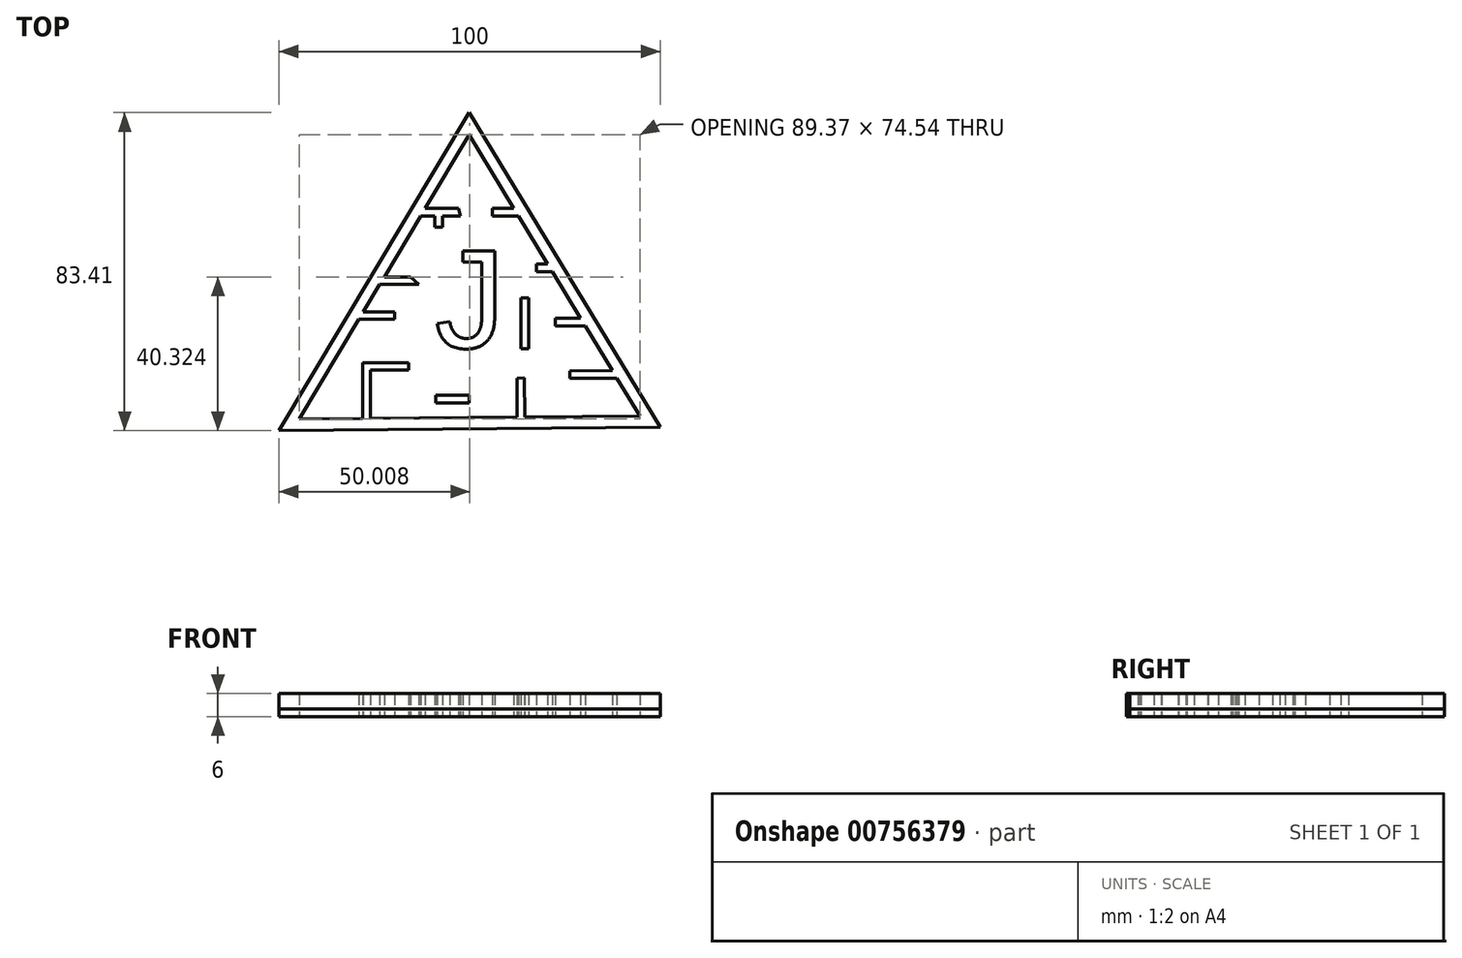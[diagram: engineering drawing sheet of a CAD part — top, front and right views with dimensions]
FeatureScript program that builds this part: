
annotation { "Feature Type Name" : "Feature", "Feature Type Description" : "" }
export const myFeature = defineFeature(function(context is Context, id is Id, definition is map)
    precondition{}
    {
        {
            var Q0;
            Q0=qCreatedBy(makeId("Top.planeOp"),FACE);
            var sketch = newSketch(context, id + "F0", { "sketchPlane" : qUnion([Q0])});
            skLineSegment(sketch, "E0.0", {"start": v(50.1, -33.95) * mm, "end": v(-49.89, -34.84) * mm});
            skLineSegment(sketch, "E0.1", {"start": v(-49.89, -34.84) * mm, "end": v(0, 48.57) * mm});
            skLineSegment(sketch, "E0.2", {"start": v(0, 48.57) * mm, "end": v(50.1, -33.95) * mm});
            skPoint(sketch, "E0.0.midPoint", {"position": v(0.11, -34.4) * mm});
            skText(sketch, "E1", { "text": "J", "fontName": "Arimo-Regular.ttf"});
            skLineSegment(sketch, "E2", {"start": v(6.14, 23.46) * mm, "end": v(11.22, 23.46) * mm});
            skLineSegment(sketch, "E3", {"start": v(-6.97, 21.46) * mm, "end": v(-6.97, 18.51) * mm});
            skLineSegment(sketch, "E4", {"start": v(-25.9, -19) * mm, "end": v(-25.9, -31.62) * mm});
            skLineSegment(sketch, "E5", {"start": v(-25.9, -19) * mm, "end": v(-15.83, -19) * mm});
            skLineSegment(sketch, "E6", {"start": v(-8.82, -25.62) * mm, "end": v(0, -25.55) * mm});
            skLineSegment(sketch, "E7", {"start": v(12.63, -31.28) * mm, "end": v(12.54, -21.07) * mm});
            skLineSegment(sketch, "E8", {"start": v(38.78, -21.07) * mm, "end": v(26.42, -21.18) * mm});
            skLineSegment(sketch, "E9", {"start": v(-15.33, 5.48) * mm, "end": v(-22.27, 5.48) * mm});
            skPoint(sketch, "E9.startSnap0", {"position": v(-22.27, 5.48) * mm});
            skLineSegment(sketch, "E10", {"start": v(15.62, 0) * mm, "end": v(15.62, -13.31) * mm});
            skLineSegment(sketch, "E11", {"start": v(17.7, 8.85) * mm, "end": v(20.6, 8.85) * mm});
            skLineSegment(sketch, "E12", {"start": v(22.63, -5.36) * mm, "end": v(29.23, -5.36) * mm});
            skLineSegment(sketch, "E13.0", {"start": v(6.14, 21.46) * mm, "end": v(12.96, 21.46) * mm});
            skLineSegment(sketch, "E14.0", {"start": v(17.7, 6.85) * mm, "end": v(20.94, 6.85) * mm});
            skLineSegment(sketch, "E15.0", {"start": v(22.63, -7.36) * mm, "end": v(29.56, -7.36) * mm});
            skLineSegment(sketch, "E16.0", {"start": v(13.62, 0) * mm, "end": v(13.62, -13.31) * mm});
            skLineSegment(sketch, "E17.0", {"start": v(37.57, -19.08) * mm, "end": v(26.4, -19.18) * mm});
            skLineSegment(sketch, "E18.0", {"start": v(14.63, -31.3) * mm, "end": v(14.54, -21.05) * mm});
            skLineSegment(sketch, "E19.0", {"start": v(-8.8, -27.62) * mm, "end": v(0.02, -27.55) * mm});
            skLineSegment(sketch, "E20.0", {"start": v(-27.9, -19) * mm, "end": v(-27.9, -31.64) * mm});
            skLineSegment(sketch, "E21.0", {"start": v(-25.5, -17) * mm, "end": v(-15.83, -17) * mm});
            skLineSegment(sketch, "E22", {"start": v(6.14, 23.46) * mm, "end": v(6.14, 21.46) * mm});
            skLineSegment(sketch, "E23.0", {"start": v(-13.24, 3.48) * mm, "end": v(-22.27, 3.48) * mm});
            skLineSegment(sketch, "E24", {"start": v(-6.97, 18.51) * mm, "end": v(-8.97, 18.51) * mm});
            skLineSegment(sketch, "E25", {"start": v(-2.3, 21.46) * mm, "end": v(-2.74, 23.46) * mm});
            skLineSegment(sketch, "E26", {"start": v(17.7, 6.85) * mm, "end": v(17.7, 8.85) * mm});
            skLineSegment(sketch, "E27", {"start": v(22.63, -5.36) * mm, "end": v(22.63, -7.36) * mm});
            skLineSegment(sketch, "E28", {"start": v(13.62, -13.31) * mm, "end": v(15.62, -13.31) * mm});
            skLineSegment(sketch, "E29", {"start": v(13.62, 0) * mm, "end": v(15.62, 0) * mm});
            skLineSegment(sketch, "E30", {"start": v(26.4, -19.18) * mm, "end": v(26.42, -21.18) * mm});
            skLineSegment(sketch, "E31", {"start": v(0, -25.55) * mm, "end": v(0.02, -27.55) * mm});
            skLineSegment(sketch, "E32", {"start": v(-8.82, -25.62) * mm, "end": v(-8.8, -27.62) * mm});
            skLineSegment(sketch, "E33", {"start": v(-27.9, -19) * mm, "end": v(-27.91, -17) * mm});
            skLineSegment(sketch, "E34", {"start": v(-27.91, -17) * mm, "end": v(-25.5, -17) * mm});
            skLineSegment(sketch, "E35", {"start": v(-15.83, -17) * mm, "end": v(-15.83, -19) * mm});
            skLineSegment(sketch, "E36", {"start": v(12.54, -21.07) * mm, "end": v(14.54, -21.05) * mm});
            skLineSegment(sketch, "E37", {"start": v(-13.24, 3.48) * mm, "end": v(-15.33, 5.48) * mm});
            skLineSegment(sketch, "E38", {"start": v(15.62, 0) * mm, "end": v(13.62, 0) * mm});
            skLineSegment(sketch, "E39", {"start": v(-27.76, -3.69) * mm, "end": v(-19.52, -3.69) * mm});
            skLineSegment(sketch, "E40.0", {"start": v(-28.13, -5.69) * mm, "end": v(-19.52, -5.69) * mm});
            skLineSegment(sketch, "E41", {"start": v(-19.52, -5.69) * mm, "end": v(-19.52, -3.69) * mm});
            skLineSegment(sketch, "E42.0", {"start": v(-44.57, -31.79) * mm, "end": v(-28.96, -5.69) * mm});
            skLineSegment(sketch, "E42.1", {"start": v(44.8, -31) * mm, "end": v(14.63, -31.26) * mm});
            skLineSegment(sketch, "E42.2", {"start": v(0.02, 42.76) * mm, "end": v(11.73, 23.46) * mm});
            skLineSegment(sketch, "E43.trimOffspring", {"start": v(-6.97, 21.46) * mm, "end": v(-2.3, 21.46) * mm});
            skLineSegment(sketch, "E44.trimOffspring", {"start": v(-8.97, 21.46) * mm, "end": v(-8.97, 18.51) * mm});
            skPoint(sketch, "E45.orphan", {"position": v(-6.97, 23.46) * mm});
            skLineSegment(sketch, "E46.trimOffspring", {"start": v(-11.52, 23.46) * mm, "end": v(0.02, 42.76) * mm});
            skPoint(sketch, "E47.orphan", {"position": v(-11.2, 23.46) * mm});
            skLineSegment(sketch, "E48", {"start": v(-2.74, 23.46) * mm, "end": v(-11.52, 23.46) * mm});
            skLineSegment(sketch, "E49", {"start": v(-8.97, 21.46) * mm, "end": v(-12.72, 21.46) * mm});
            skLineSegment(sketch, "E50", {"start": v(11.22, 23.46) * mm, "end": v(11.73, 23.46) * mm});
            skLineSegment(sketch, "E51", {"start": v(-22.27, 3.48) * mm, "end": v(-23.47, 3.48) * mm});
            skLineSegment(sketch, "E52", {"start": v(20.94, 6.85) * mm, "end": v(21.82, 6.85) * mm});
            skLineSegment(sketch, "E53.trimOffspring", {"start": v(21.82, 6.85) * mm, "end": v(29.23, -5.36) * mm});
            skLineSegment(sketch, "E54.trimOffspring", {"start": v(-22.27, 5.48) * mm, "end": v(-12.72, 21.46) * mm});
            skLineSegment(sketch, "E55", {"start": v(-28.13, -5.69) * mm, "end": v(-28.96, -5.69) * mm});
            skLineSegment(sketch, "E56.trimOffspring", {"start": v(-27.76, -3.69) * mm, "end": v(-23.47, 3.48) * mm});
            skLineSegment(sketch, "E57", {"start": v(29.56, -7.36) * mm, "end": v(30.45, -7.36) * mm});
            skLineSegment(sketch, "E58.trimOffspring", {"start": v(30.45, -7.36) * mm, "end": v(37.57, -19.08) * mm});
            skLineSegment(sketch, "E59.trimOffspring", {"start": v(12.63, -31.28) * mm, "end": v(-25.9, -31.62) * mm});
            skLineSegment(sketch, "E60.trimOffspring", {"start": v(-27.9, -31.64) * mm, "end": v(-44.57, -31.79) * mm});
            skLineSegment(sketch, "E61.trimOffspring", {"start": v(38.78, -21.07) * mm, "end": v(44.8, -31) * mm});
            skLineSegment(sketch, "E62.trimOffspring", {"start": v(12.95, 21.46) * mm, "end": v(20.6, 8.85) * mm});
            const initialGuessF0  = {"E1": [-0.00901, -0.01312, 1, 0, 0.02652]};
            skSetInitialGuess(sketch, initialGuessF0);
            skSolve(sketch);
        }
        {
            var Q0;
            Q0=makeQuery(id+"F0.imprint","IMPRINT",FACE,{"disambiguationData":[TD([[makeQuery(id+"F0.imprint","IMPRINT",EDGE,{"derivedFrom":sQuery(id+"F0.wireOp",EDGE,"E1.sketch_text.stroke-0")}),-1.0]])]});
            var Q1;
            Q1=makeQuery(id+"F0.imprint","IMPRINT",FACE,{"disambiguationData":[TD([[makeQuery(id+"F0.imprint","IMPRINT",EDGE,{"derivedFrom":sQuery(id+"F0.wireOp",EDGE,"E0.0")}),-1.0]])]});
            var Q2;
            Q2=makeQuery(id+"F0.imprint","IMPRINT",FACE,{"disambiguationData":[TD([[makeQuery(id+"F0.imprint","IMPRINT",EDGE,{"derivedFrom":sQuery(id+"F0.wireOp",EDGE,"E10")}),-1.0]])]});
            var Q3;
            Q3=makeQuery(id+"F0.imprint","IMPRINT",FACE,{"disambiguationData":[TD([[makeQuery(id+"F0.imprint","IMPRINT",EDGE,{"derivedFrom":sQuery(id+"F0.wireOp",EDGE,"E6")}),-1.0]])]});
            extrude(context, id + "F1", {"entities" : qUnion([Q0, Q1, Q2, Q3]), "depth" : 6 * mm, "offsetDistance" : 25 * mm});
        }
        {
            var Q0;
            Q0=qCreatedBy(makeId("Top.planeOp"),FACE);
            var sketch = newSketch(context, id + "F2", { "sketchPlane" : qUnion([Q0])});
            skLineSegment(sketch, "E63.0", {"start": v(50.1, -33.95) * mm, "end": v(-49.89, -34.84) * mm});
            skLineSegment(sketch, "E64.0", {"start": v(-49.89, -34.84) * mm, "end": v(0, 48.57) * mm});
            skLineSegment(sketch, "E65.0", {"start": v(0, 48.57) * mm, "end": v(50.1, -33.95) * mm});
            skSolve(sketch);
        }
        {
            var Q0;
            Q0 = qSketchRegion(id + "F2", true);
            extrude(context, id + "F3", {"entities" : qUnion([Q0]), "depth" : 2 * mm, "offsetDistance" : 25 * mm});
        }
    });
